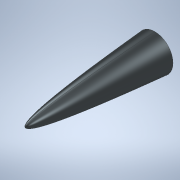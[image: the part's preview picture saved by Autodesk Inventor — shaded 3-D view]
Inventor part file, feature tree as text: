
AUTODESK INVENTOR PART (.ipt)
format: ipt  version: 2020 (Build 240168000, 168)  size: 204,800 bytes
history: native  units: mm
features: revolve x1, sketch x1
ambient origin geometry x8: Origin, YZ Plane, XZ Plane, XY Plane, X Axis, Y Axis, Z Axis, Center Point
bodies: Body1 (feature_tree)
feature tree (2):
  revolve  "Revolution4"  [1 undecoded]
  sketch  "Sketch1"  dims[d44=10.0mm d55=1.8mm d57=120.0mm d58=118.2mm d59=16.8mm d60=90.0deg d11=0.872665mm d12=0.872665mm]
note: 1 required parameter value undecoded (feature->parameter linkage not recoverable at this tier; creation-order binding heuristic only, values carry confidence <= 0.55)
